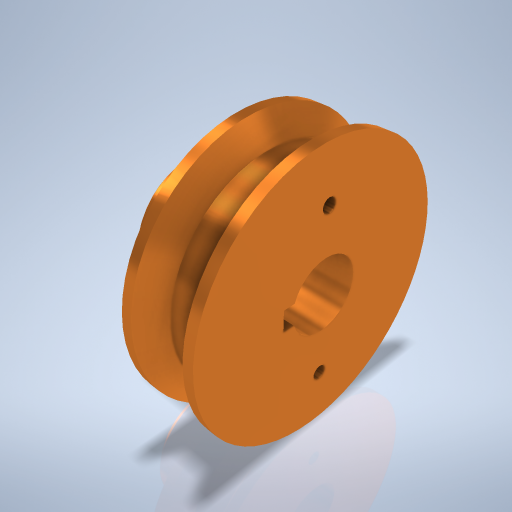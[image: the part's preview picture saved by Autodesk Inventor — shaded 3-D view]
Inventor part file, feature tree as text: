
AUTODESK INVENTOR PART (.ipt)
format: ipt  version: 2024.2 (Build 282272000, 272)  size: 325,120 bytes
history: native  units: mm
features: sketch x5, hole x3, revolve x1, chamfer x1, extrude x1, plane x1, mirror x1
ambient origin geometry x8: Origin, YZ Plane, XZ Plane, XY Plane, X Axis, Y Axis, Z Axis, Center Point
bodies: Volumenkörper1 (feature_tree)
feature tree (13):
  revolve  "Umdrehung1"
  chamfer  "Fasen1"  Distance=20.0mm
  hole  "Bohrung1"  [1 undecoded]
  extrude  "Extrusion1"  Depth=5.0mm
  plane  "Arbeitsebene1"
  hole  "Bohrung2"  [1 undecoded]
  mirror  "Spiegeln1"
  hole  "Bohrung3"  [1 undecoded]
  sketch  "Skizze1"  dims[d0=21.0mm]
  sketch  "Skizze2"  dims[d1=60.0deg]
  sketch  "Skizze3"  dims[d2=1.5mm]
  sketch  "Skizze4"  dims[d3=1.5mm]
  sketch  "Skizze5"  dims[d4=10.0mm d5=20.0mm d6=31.0mm d7=38.0mm d8=90.0deg d9=1.0mm d10=2.0mm d11=45.0deg d12=10.0mm d13=6.0mm d14=4.0mm d15=2.0mm d16=90.0deg d17=8.0mm d18=0.0mm d19=3.0mm d20=11.4mm d21=10.0mm d22=0.0mm d23=0.0mm d24=5.0mm d25=2.459mm d26=6.0mm d27=4.0mm d28=2.0mm d29=90.0deg d30=8.0mm d31=0.0mm d32=23.0mm d33=2.0mm d34=6.0mm d35=4.0mm d36=2.0mm d37=90.0deg d38=6.0mm d39=20.594885mm]
note: 3 required parameter values undecoded (feature->parameter linkage not recoverable at this tier; creation-order binding heuristic only, values carry confidence <= 0.55)
